# Revit family: NLRS_33_WI_FLB_maatwerk vloerluik Linfi_lin
name_source: partatom
category: Windows
units: mm (PartAtom-declared; Revit-internal decimal feet)

## family parameters
Always vertical = No
Cut with Voids When Loaded = Yes
Host = Floor
Room Calculation Point = No
Shared = Yes

## types (2) — shared parameters
Analytic Construction = <None>
Assembly Code = 33.21
Description = Maatwerk vloerluik Linfi
IfcExportAs = IfcWindow
IfcExportType = Floor
IsExternal = No
LoadBearing = No
Manufacturer = Linfi
NLRS_C_fabrikant = Linfi Vloerluiken Ede
Type Comments = breedte maximaal 1000mm, lengte maximaal 2400mm
URL = https://linfi.nl
zero-valued in all types: Height, Width

## per-type parameters (varying)
| type | Model | NLRS_C_model |
| paneel multiplex | Maatwerk luik voorzien van multiplex | Maatwerk luik voorzien van multiplex |
| paneel glas | Maatwerk luik voorzien van geharde beglazing of multiplex | Maatwerk luik voorzien van geharde beglazing of multiplex |

type visibility flags: 2 boolean params named "<type name>" — each type sets only its own to Yes (folded from table)

## geometry (parser evidence)
native form markers: Blend x14, Sweep x11
no freeform markers — native parametric forms only
